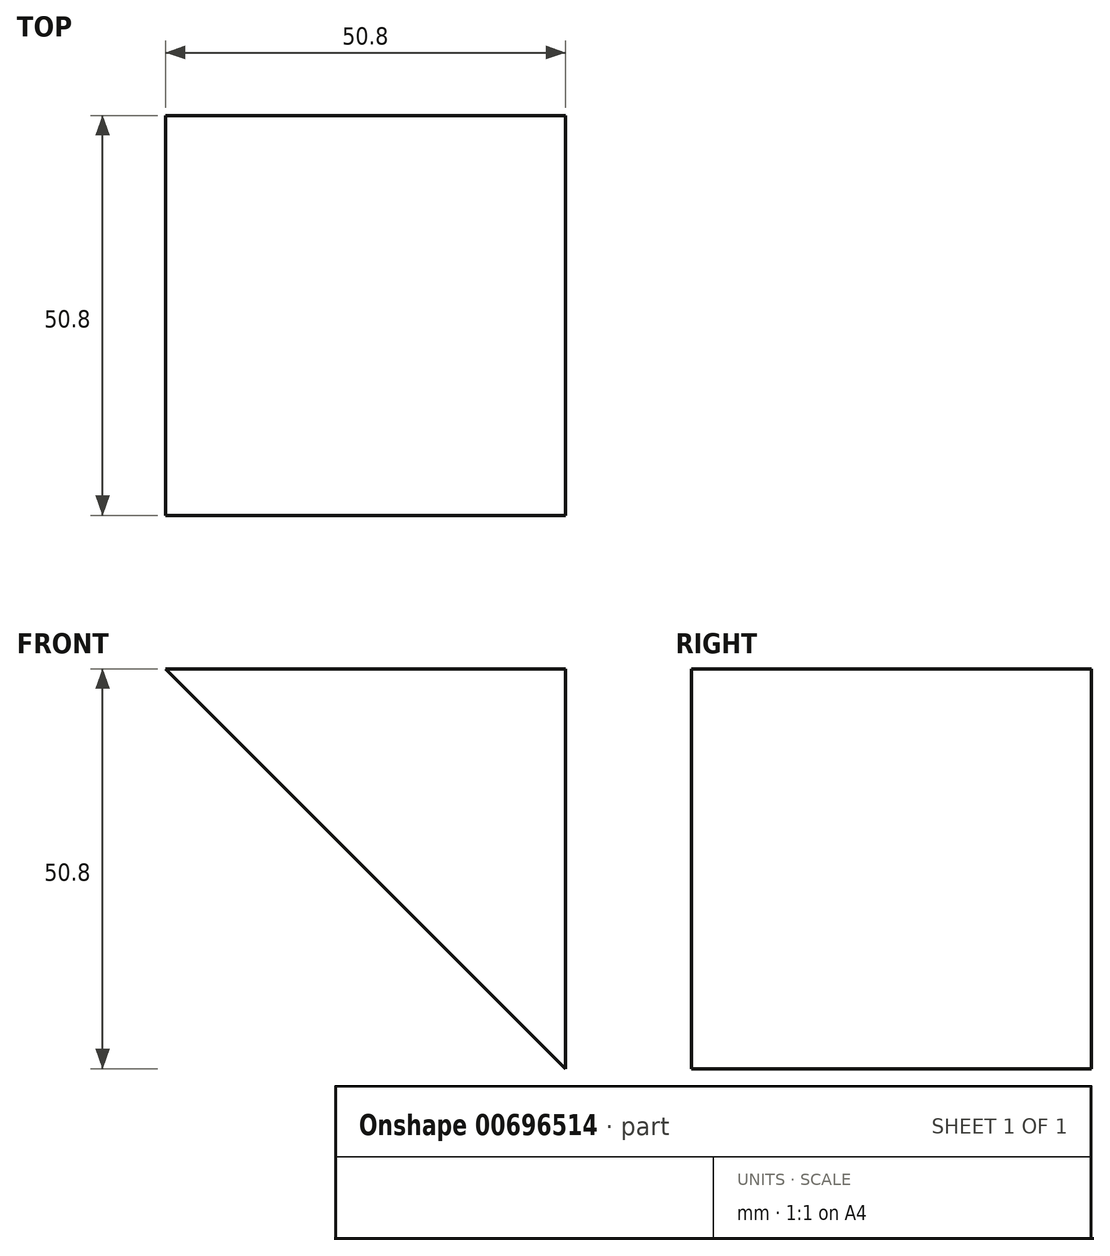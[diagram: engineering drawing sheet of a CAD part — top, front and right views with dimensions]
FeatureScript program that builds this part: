
annotation { "Feature Type Name" : "Feature", "Feature Type Description" : "" }
export const myFeature = defineFeature(function(context is Context, id is Id, definition is map)
    precondition{}
    {
        {
            var Q0;
            Q0=qCreatedBy(makeId("Front.planeOp"),FACE);
            var sketch = newSketch(context, id + "F0", { "sketchPlane" : qUnion([Q0])});
            skLineSegment(sketch, "E0", {"start": v(0, 0) * mm, "end": v(50.8, 0) * mm});
            skLineSegment(sketch, "E1", {"start": v(50.8, 0) * mm, "end": v(50.8, -50.8) * mm});
            skLineSegment(sketch, "E2", {"start": v(50.8, -50.8) * mm, "end": v(0, 0) * mm});
            skSolve(sketch);
        }
        {
            var Q0;
            Q0 = qSketchRegion(id + "F0", true);
            extrude(context, id + "F1", {"entities" : qUnion([Q0]), "depth" : 50.8 * mm, "offsetDistance" : 25.4 * mm});
        }
    });
